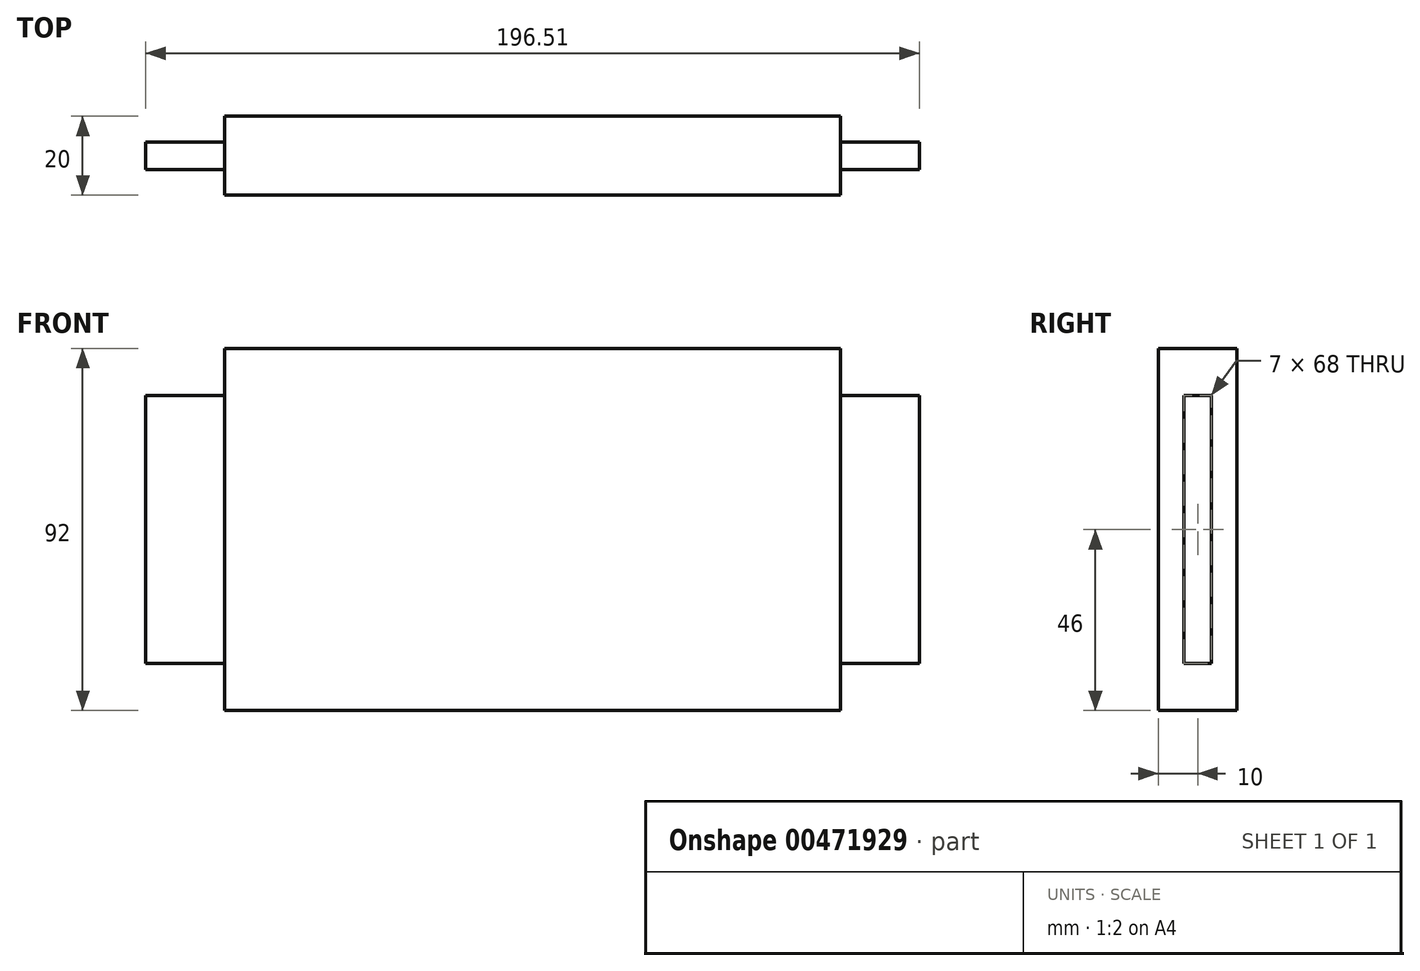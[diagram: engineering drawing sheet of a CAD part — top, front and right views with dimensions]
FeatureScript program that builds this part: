
annotation { "Feature Type Name" : "Feature", "Feature Type Description" : "" }
export const myFeature = defineFeature(function(context is Context, id is Id, definition is map)
    precondition{}
    {
        {
            var Q0;
            Q0=qCreatedBy(makeId("Front.planeOp"),FACE);
            var sketch = newSketch(context, id + "F0", { "sketchPlane" : qUnion([Q0])});
            skLineSegment(sketch, "E0", {"start": v(-56.8, -12.6) * mm, "end": v(-56.8, 55.4) * mm});
            skLineSegment(sketch, "E1", {"start": v(-36.8, 67.4) * mm, "end": v(119.7, 67.4) * mm});
            skLineSegment(sketch, "E2", {"start": v(139.7, 55.4) * mm, "end": v(139.7, -12.6) * mm});
            skLineSegment(sketch, "E3", {"start": v(119.7, -24.6) * mm, "end": v(-36.8, -24.6) * mm});
            skLineSegment(sketch, "E4", {"start": v(-36.8, 67.4) * mm, "end": v(-36.8, 55.4) * mm});
            skLineSegment(sketch, "E5", {"start": v(-36.8, 55.4) * mm, "end": v(-56.8, 55.4) * mm});
            skLineSegment(sketch, "E6", {"start": v(-36.8, -24.6) * mm, "end": v(-36.8, -12.6) * mm});
            skLineSegment(sketch, "E7", {"start": v(-36.8, -12.6) * mm, "end": v(-56.8, -12.6) * mm});
            skPoint(sketch, "E8.orphan", {"position": v(-56.8, -24.6) * mm});
            skLineSegment(sketch, "E9", {"start": v(119.7, 67.4) * mm, "end": v(119.7, 55.4) * mm});
            skLineSegment(sketch, "E10", {"start": v(119.7, 55.4) * mm, "end": v(139.7, 55.4) * mm});
            skLineSegment(sketch, "E11", {"start": v(119.7, -24.6) * mm, "end": v(119.7, -12.6) * mm});
            skLineSegment(sketch, "E12", {"start": v(119.7, -12.6) * mm, "end": v(139.7, -12.6) * mm});
            skPoint(sketch, "E13.orphan", {"position": v(139.7, -24.6) * mm});
            skSolve(sketch);
        }
        {
            var Q0;
            Q0 = qSketchRegion(id + "F0", true);
            extrude(context, id + "F1", {"entities" : qUnion([Q0]), "depth" : 20 * mm});
        }
        {
            var Q0;
            Q0=makeQuery(id+"F1.opExtrude","CAP_FACE",FACE,{"disambiguationData":[OSD([sQuery(id+"F0.wireOp",EDGE,"E0"),sQuery(id+"F0.wireOp",EDGE,"E1"),sQuery(id+"F0.wireOp",EDGE,"E2"),sQuery(id+"F0.wireOp",EDGE,"E3"),sQuery(id+"F0.wireOp",EDGE,"E4"),sQuery(id+"F0.wireOp",EDGE,"E5"),sQuery(id+"F0.wireOp",EDGE,"E6"),sQuery(id+"F0.wireOp",EDGE,"E7"),sQuery(id+"F0.wireOp",EDGE,"E9"),sQuery(id+"F0.wireOp",EDGE,"E10"),sQuery(id+"F0.wireOp",EDGE,"E11"),sQuery(id+"F0.wireOp",EDGE,"E12")])],"isStart":false});
            var sketch = newSketch(context, id + "F2", { "sketchPlane" : qUnion([Q0])});
            skLineSegment(sketch, "E14", {"start": v(119.7, 55.4) * mm, "end": v(119.7, -12.6) * mm});
            skLineSegment(sketch, "E15", {"start": v(119.7, -12.6) * mm, "end": v(139.7, -12.6) * mm});
            skLineSegment(sketch, "E16", {"start": v(139.7, -12.6) * mm, "end": v(139.7, 55.4) * mm});
            skLineSegment(sketch, "E17", {"start": v(139.7, 55.4) * mm, "end": v(119.7, 55.4) * mm});
            skLineSegment(sketch, "E18.MirrorCS", {"start": v(-56.8, 55.4) * mm, "end": v(-36.8, 55.4) * mm});
            skLineSegment(sketch, "E19.MirrorCS", {"start": v(-36.8, 55.4) * mm, "end": v(-36.8, -12.6) * mm});
            skLineSegment(sketch, "E20.MirrorCS", {"start": v(-56.8, -12.6) * mm, "end": v(-56.8, 55.4) * mm});
            skLineSegment(sketch, "E21.MirrorCS", {"start": v(-36.8, -12.6) * mm, "end": v(-56.8, -12.6) * mm});
            skSolve(sketch);
        }
        {
            var Q0;
            Q0 = qSketchRegion(id + "F2", true);
            extrude(context, id + "F3", {"entities" : qUnion([Q0]), "operationType" : NewBodyOperationType.REMOVE, "oppositeDirection" : true, "depth" : 6.5 * mm});
        }
        {
            var Q0;
            Q0=makeQuery(id+"F1.opExtrude","CAP_FACE",FACE,{"disambiguationData":[OSD([sQuery(id+"F0.wireOp",EDGE,"E0"),sQuery(id+"F0.wireOp",EDGE,"E1"),sQuery(id+"F0.wireOp",EDGE,"E2"),sQuery(id+"F0.wireOp",EDGE,"E3"),sQuery(id+"F0.wireOp",EDGE,"E4"),sQuery(id+"F0.wireOp",EDGE,"E5"),sQuery(id+"F0.wireOp",EDGE,"E6"),sQuery(id+"F0.wireOp",EDGE,"E7"),sQuery(id+"F0.wireOp",EDGE,"E9"),sQuery(id+"F0.wireOp",EDGE,"E10"),sQuery(id+"F0.wireOp",EDGE,"E11"),sQuery(id+"F0.wireOp",EDGE,"E12")])],"isStart":true});
            var sketch = newSketch(context, id + "F4", { "sketchPlane" : qUnion([Q0])});
            skLineSegment(sketch, "E22", {"start": v(-119.7, 55.4) * mm, "end": v(-119.7, -12.6) * mm});
            skLineSegment(sketch, "E23", {"start": v(-119.7, -12.6) * mm, "end": v(-139.7, -12.6) * mm});
            skLineSegment(sketch, "E24", {"start": v(-139.7, -12.6) * mm, "end": v(-139.7, 55.4) * mm});
            skLineSegment(sketch, "E25", {"start": v(-139.7, 55.4) * mm, "end": v(-119.7, 55.4) * mm});
            skLineSegment(sketch, "E26", {"start": v(-41.45, 67.4) * mm, "end": v(-41.45, -24.6) * mm});
            skLineSegment(sketch, "E27.MirrorCS", {"start": v(56.8, 55.4) * mm, "end": v(36.8, 55.4) * mm});
            skLineSegment(sketch, "E28.MirrorCS", {"start": v(36.8, 55.4) * mm, "end": v(36.8, -12.6) * mm});
            skLineSegment(sketch, "E29.MirrorCS", {"start": v(56.8, -12.6) * mm, "end": v(56.8, 55.4) * mm});
            skLineSegment(sketch, "E30.MirrorCS", {"start": v(36.8, -12.6) * mm, "end": v(56.8, -12.6) * mm});
            skSolve(sketch);
        }
        {
            var Q0;
            Q0 = qSketchRegion(id + "F4", true);
            extrude(context, id + "F5", {"entities" : qUnion([Q0]), "operationType" : NewBodyOperationType.REMOVE, "oppositeDirection" : true, "depth" : 6.5 * mm});
        }
    });
